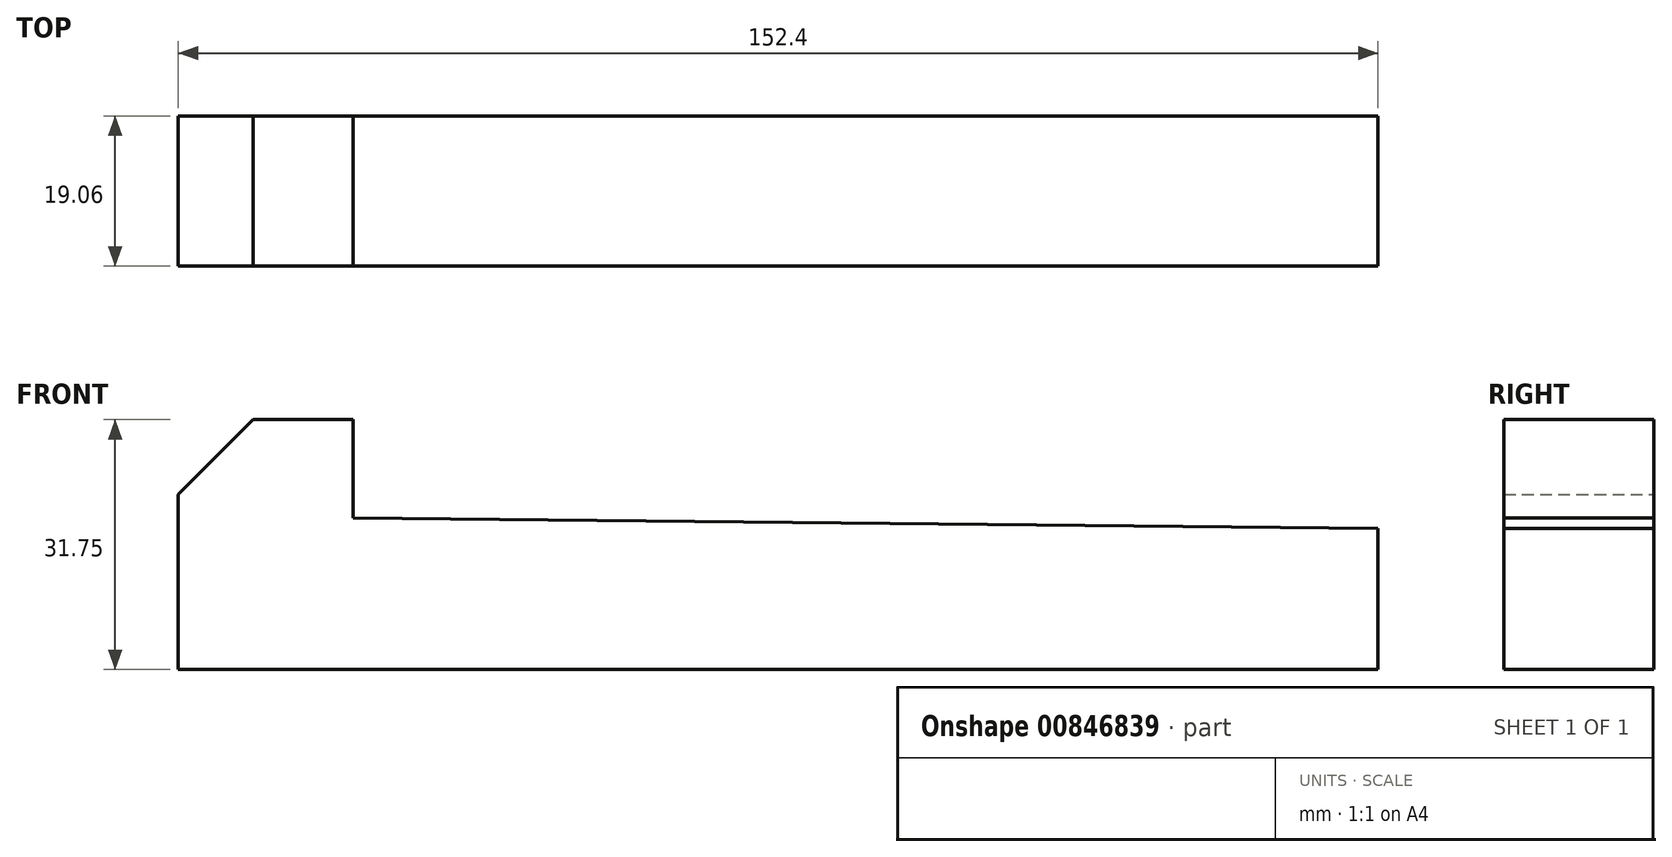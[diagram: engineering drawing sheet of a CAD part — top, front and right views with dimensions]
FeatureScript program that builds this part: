
annotation { "Feature Type Name" : "Feature", "Feature Type Description" : "" }
export const myFeature = defineFeature(function(context is Context, id is Id, definition is map)
    precondition{}
    {
        {
            var Q0;
            Q0=qCreatedBy(makeId("Front.planeOp"),FACE);
            var sketch = newSketch(context, id + "F0", { "sketchPlane" : qUnion([Q0])});
            skLineSegment(sketch, "E0", {"start": v(-76.2, 0) * mm, "end": v(76.2, 0) * mm});
            skLineSegment(sketch, "E1", {"start": v(-76.2, 0) * mm, "end": v(-76.2, 22.22) * mm});
            skLineSegment(sketch, "E2", {"start": v(-76.2, 22.22) * mm, "end": v(-66.68, 31.75) * mm});
            skLineSegment(sketch, "E3", {"start": v(-66.68, 31.75) * mm, "end": v(-53.98, 31.75) * mm});
            skLineSegment(sketch, "E4", {"start": v(-53.98, 31.75) * mm, "end": v(-53.98, 19.25) * mm});
            skLineSegment(sketch, "E5", {"start": v(-53.97, 19.25) * mm, "end": v(76.2, 17.9) * mm});
            skLineSegment(sketch, "E6", {"start": v(76.2, 17.9) * mm, "end": v(76.2, 0) * mm});
            skLineSegment(sketch, "E7", {"start": v(-34.93, 19.05) * mm, "end": v(-34.93, 0) * mm, "construction": true});
            skSolve(sketch);
        }
        {
            var Q0;
            Q0 = qSketchRegion(id + "F0", true);
            extrude(context, id + "F1", {"entities" : qUnion([Q0]), "depth" : 19.05 * mm, "offsetDistance" : 25.4 * mm, "symmetric" : true});
        }
    });
